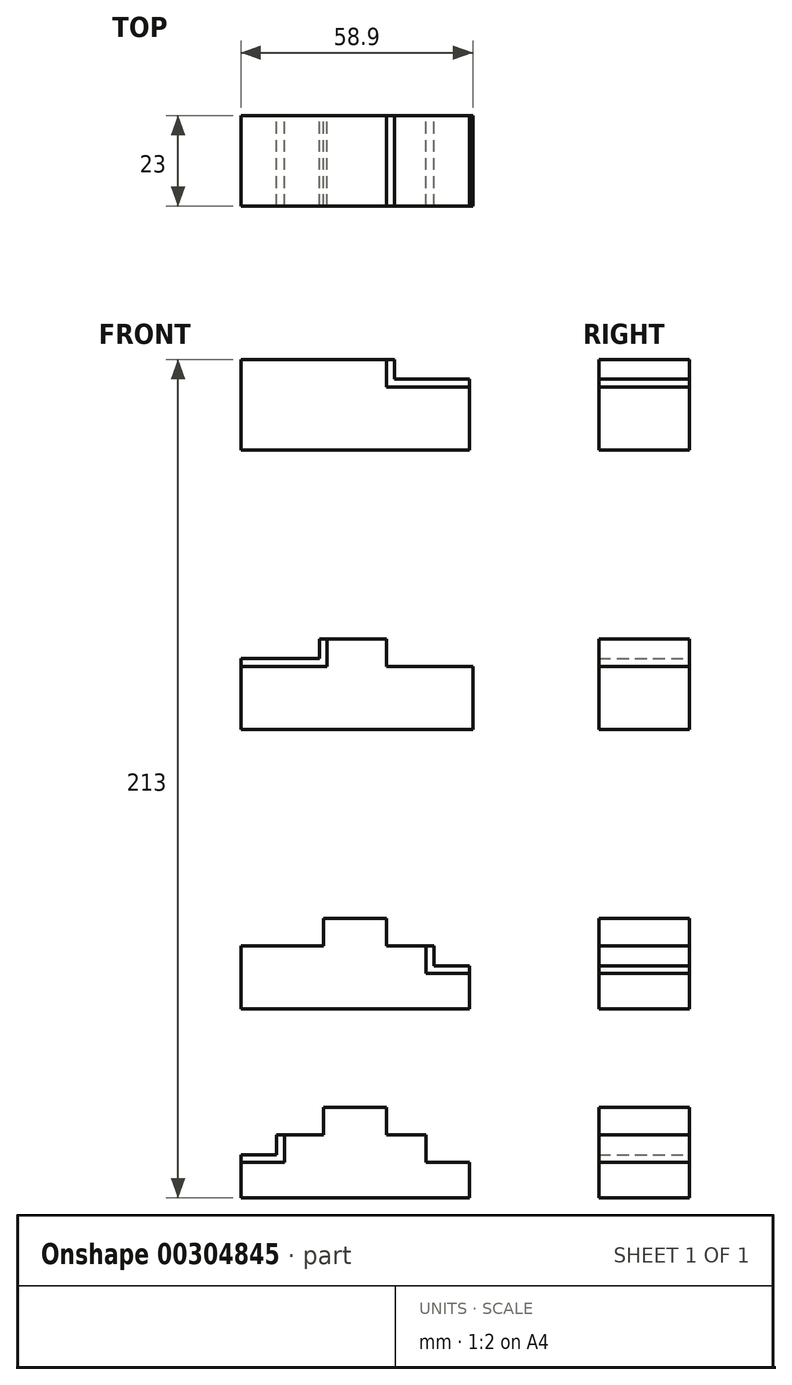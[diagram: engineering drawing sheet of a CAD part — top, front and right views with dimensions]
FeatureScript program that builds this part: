
annotation { "Feature Type Name" : "Feature", "Feature Type Description" : "" }
export const myFeature = defineFeature(function(context is Context, id is Id, definition is map)
    precondition{}
    {
        {
            var Q0;
            Q0=qCreatedBy(makeId("Front.planeOp"),FACE);
            var sketch = newSketch(context, id + "F0", { "sketchPlane" : qUnion([Q0])});
            skLineSegment(sketch, "E0.bottom", {"start": v(0, 0) * mm, "end": v(200, 0) * mm, "construction": true});
            skLineSegment(sketch, "E0.top", {"start": v(0, 300) * mm, "end": v(200, 300) * mm, "construction": true});
            skLineSegment(sketch, "E0.left", {"start": v(0, 0) * mm, "end": v(0, 300) * mm, "construction": true});
            skLineSegment(sketch, "E0.right", {"start": v(200, 0) * mm, "end": v(200, 300) * mm, "construction": true});
            skPoint(sketch, "E1", {"position": v(0, 200) * mm});
            skPoint(sketch, "E2", {"position": v(0, 100) * mm});
            skSolve(sketch);
        }
        {
            var Q0;
            Q0=qCreatedBy(makeId("Front.planeOp"),FACE);
            var sketch = newSketch(context, id + "F1", { "sketchPlane" : qUnion([Q0])});
            skLineSegment(sketch, "E3.bottom", {"start": v(30, 252) * mm, "end": v(88, 252) * mm});
            skLineSegment(sketch, "E3.top", {"start": v(30, 229) * mm, "end": v(88, 229) * mm});
            skLineSegment(sketch, "E3.left", {"start": v(30, 252) * mm, "end": v(30, 229) * mm});
            skLineSegment(sketch, "E3.right", {"start": v(88, 252) * mm, "end": v(88, 229) * mm});
            skLineSegment(sketch, "E4", {"start": v(69, 252) * mm, "end": v(69, 247) * mm});
            skLineSegment(sketch, "E5", {"start": v(69, 247) * mm, "end": v(88, 247) * mm});
            skLineSegment(sketch, "E6.0", {"start": v(67, 245) * mm, "end": v(88, 245) * mm});
            skLineSegment(sketch, "E6.1", {"start": v(67, 252) * mm, "end": v(67, 245) * mm});
            skSolve(sketch);
        }
        {
            var Q0;
            Q0=qCreatedBy(makeId("Front.planeOp"),FACE);
            var sketch = newSketch(context, id + "F2", { "sketchPlane" : qUnion([Q0])});
            skLineSegment(sketch, "E7.bottom", {"start": v(30, 181) * mm, "end": v(88.9, 181) * mm});
            skLineSegment(sketch, "E7.top", {"start": v(30, 158) * mm, "end": v(88.9, 158) * mm});
            skLineSegment(sketch, "E7.left", {"start": v(30, 181) * mm, "end": v(30, 158) * mm});
            skLineSegment(sketch, "E7.right", {"start": v(88.9, 181) * mm, "end": v(88.9, 158) * mm});
            skLineSegment(sketch, "E8", {"start": v(30, 176) * mm, "end": v(49.9, 176) * mm});
            skLineSegment(sketch, "E9", {"start": v(49.9, 176) * mm, "end": v(49.9, 181) * mm});
            skLineSegment(sketch, "E10.0", {"start": v(51.9, 174) * mm, "end": v(51.9, 181) * mm});
            skLineSegment(sketch, "E10.1", {"start": v(30, 174) * mm, "end": v(51.9, 174) * mm});
            skLineSegment(sketch, "E11", {"start": v(59.45, 154.93) * mm, "end": v(59.45, 132.57) * mm, "construction": true});
            skPoint(sketch, "E11.startSnap0", {"position": v(59.45, 158) * mm});
            skLineSegment(sketch, "E12.MirrorCS", {"start": v(67, 174) * mm, "end": v(67, 181) * mm});
            skLineSegment(sketch, "E13.MirrorCS", {"start": v(88.9, 174) * mm, "end": v(67, 174) * mm});
            skSolve(sketch);
        }
        {
            var Q0;
            Q0=qCreatedBy(makeId("Front.planeOp"),FACE);
            var sketch = newSketch(context, id + "F3", { "sketchPlane" : qUnion([Q0])});
            skLineSegment(sketch, "E14.bottom", {"start": v(30, 110) * mm, "end": v(88, 110) * mm});
            skLineSegment(sketch, "E14.top", {"start": v(30, 87) * mm, "end": v(88, 87) * mm});
            skLineSegment(sketch, "E14.left", {"start": v(30, 110) * mm, "end": v(30, 87) * mm});
            skLineSegment(sketch, "E14.right", {"start": v(88, 110) * mm, "end": v(88, 87) * mm});
            skLineSegment(sketch, "E15", {"start": v(67, 110) * mm, "end": v(67, 103) * mm});
            skLineSegment(sketch, "E16", {"start": v(67, 103) * mm, "end": v(77, 103) * mm});
            skLineSegment(sketch, "E17", {"start": v(77, 103) * mm, "end": v(77, 96) * mm});
            skLineSegment(sketch, "E18", {"start": v(77, 96) * mm, "end": v(88, 96) * mm});
            skLineSegment(sketch, "E19.0", {"start": v(79, 98) * mm, "end": v(88, 98) * mm});
            skLineSegment(sketch, "E19.1", {"start": v(79, 105) * mm, "end": v(79, 98) * mm});
            skLineSegment(sketch, "E19.2", {"start": v(69, 105) * mm, "end": v(79, 105) * mm});
            skLineSegment(sketch, "E19.3", {"start": v(69, 110.26) * mm, "end": v(69, 105) * mm});
            skLineSegment(sketch, "E20", {"start": v(77, 103) * mm, "end": v(79, 103) * mm});
            skLineSegment(sketch, "E21", {"start": v(59, 115.4) * mm, "end": v(59, 121.32) * mm, "construction": true});
            skPoint(sketch, "E21.startSnap0", {"position": v(59, 110) * mm});
            skLineSegment(sketch, "E22.MirrorCS", {"start": v(51, 110) * mm, "end": v(51, 103) * mm});
            skLineSegment(sketch, "E23.MirrorCS", {"start": v(51, 103) * mm, "end": v(41, 103) * mm});
            skLineSegment(sketch, "E24.MirrorCS", {"start": v(41, 103) * mm, "end": v(41, 96) * mm, "construction": true});
            skLineSegment(sketch, "E25.MirrorCS", {"start": v(41, 96) * mm, "end": v(30, 96) * mm});
            skLineSegment(sketch, "E26", {"start": v(41, 103) * mm, "end": v(30, 103) * mm});
            skLineSegment(sketch, "E27.0.1.0", {"start": v(41, 55) * mm, "end": v(41, 48) * mm});
            skLineSegment(sketch, "E27.0.1.1", {"start": v(67, 55) * mm, "end": v(77, 55) * mm});
            skLineSegment(sketch, "E27.0.1.2", {"start": v(77, 48) * mm, "end": v(88, 48) * mm});
            skLineSegment(sketch, "E27.0.1.3", {"start": v(51, 62) * mm, "end": v(51, 55) * mm});
            skLineSegment(sketch, "E27.0.1.4", {"start": v(30, 62) * mm, "end": v(88, 62) * mm});
            skLineSegment(sketch, "E27.0.1.5", {"start": v(51, 55) * mm, "end": v(41, 55) * mm});
            skPoint(sketch, "E27.0.1.6", {"position": v(59, 62) * mm});
            skLineSegment(sketch, "E27.0.1.7", {"start": v(30, 39) * mm, "end": v(88, 39) * mm});
            skLineSegment(sketch, "E27.0.1.8", {"start": v(88, 62) * mm, "end": v(88, 39) * mm});
            skLineSegment(sketch, "E27.0.1.9", {"start": v(30, 62) * mm, "end": v(30, 39) * mm});
            skLineSegment(sketch, "E27.0.1.10", {"start": v(41, 55) * mm, "end": v(30, 55) * mm, "construction": true});
            skLineSegment(sketch, "E27.0.1.11", {"start": v(79, 50) * mm, "end": v(88, 50) * mm});
            skLineSegment(sketch, "E27.0.1.12", {"start": v(69, 57) * mm, "end": v(79, 57) * mm});
            skLineSegment(sketch, "E27.0.1.13", {"start": v(41, 48) * mm, "end": v(30, 48) * mm});
            skLineSegment(sketch, "E27.0.1.14", {"start": v(67, 62) * mm, "end": v(67, 55) * mm});
            skLineSegment(sketch, "E27.0.1.15", {"start": v(69, 62.26) * mm, "end": v(69, 57) * mm});
            skLineSegment(sketch, "E27.0.1.16", {"start": v(77, 55) * mm, "end": v(77, 48) * mm});
            skLineSegment(sketch, "E27.0.1.17", {"start": v(79, 57) * mm, "end": v(79, 50) * mm});
            skLineSegment(sketch, "E27.0.1.18", {"start": v(77, 55) * mm, "end": v(79, 55) * mm});
            skLineSegment(sketch, "E27.direction1", {"start": v(30, 87) * mm, "end": v(120.8, 87) * mm, "construction": true});
            skLineSegment(sketch, "E27.direction2", {"start": v(30, 87) * mm, "end": v(30, 39) * mm, "construction": true});
            skLineSegment(sketch, "E28.MirrorCS", {"start": v(39, 57) * mm, "end": v(39, 50) * mm});
            skLineSegment(sketch, "E29.MirrorCS", {"start": v(49, 62.26) * mm, "end": v(49, 57) * mm});
            skLineSegment(sketch, "E30.MirrorCS", {"start": v(39, 50) * mm, "end": v(30, 50) * mm});
            skLineSegment(sketch, "E31.MirrorCS", {"start": v(41, 55) * mm, "end": v(39, 55) * mm});
            skLineSegment(sketch, "E32.MirrorCS", {"start": v(49, 57) * mm, "end": v(39, 57) * mm});
            skSolve(sketch);
        }
        {
            var Q0;
            Q0=makeQuery(id+"F1.imprint","IMPRINT",FACE,{"disambiguationData":[TD([[makeQuery(id+"F1.imprint","IMPRINT",EDGE,{"derivedFrom":sQuery(id+"F1.wireOp",EDGE,"K7ecBAno-6BI1-ZI8E-EF1z-YLERG8wcsJRb.bottom")}),-1.0]])]});
            var Q1;
            {var subQ1=sQuery(id+"F2.wireOp",EDGE,"E7.top");Q1=makeQuery(id+"F2.imprint","IMPRINT",FACE,{"disambiguationData":[TD([[makeQuery(id+"F2.imprint","IMPRINT",EDGE,{"derivedFrom":subQ1}),1.0]])]});}
            var Q2;
            {var subQ1=sQuery(id+"F1.wireOp",EDGE,"E3.top");Q2=makeQuery(id+"F1.imprint","IMPRINT",FACE,{"disambiguationData":[TD([[makeQuery(id+"F1.imprint","IMPRINT",EDGE,{"derivedFrom":subQ1}),1.0]])]});}
            var Q3;
            {var subQ5=sQuery(id+"F3.wireOp",EDGE,"E14.top");Q3=makeQuery(id+"F3.imprint","IMPRINT",FACE,{"disambiguationData":[TD([[makeQuery(id+"F3.imprint","IMPRINT",EDGE,{"derivedFrom":subQ5}),1.0]])]});}
            var Q4;
            Q4=makeQuery(id+"F3.imprint","IMPRINT",FACE,{"disambiguationData":[TD([[makeQuery(id+"F3.imprint","IMPRINT",EDGE,{"derivedFrom":sQuery(id+"F3.wireOp",EDGE,"E27.0.1.0")}),1.0]])]});
            extrude(context, id + "F4", {"entities" : qUnion([Q0, Q1, Q2, Q3, Q4]), "depth" : 23 * mm});
        }
        {
            var Q0;
            {var subQ0=sQuery(id+"F2.wireOp",EDGE,"E8");Q0=makeQuery(id+"F2.imprint","IMPRINT",FACE,{"disambiguationData":[TD([[makeQuery(id+"F2.imprint","IMPRINT",EDGE,{"derivedFrom":subQ0}),-1.0]])]});}
            var Q1;
            Q1=makeQuery(id+"F3.imprint","IMPRINT",FACE,{"disambiguationData":[TD([[makeQuery(id+"F3.imprint","IMPRINT",EDGE,{"derivedFrom":sQuery(id+"F3.wireOp",EDGE,"E17")}),1.0]])]});
            var Q2;
            Q2=makeQuery(id+"F3.imprint","IMPRINT",FACE,{"disambiguationData":[TD([[makeQuery(id+"F3.imprint","IMPRINT",EDGE,{"derivedFrom":sQuery(id+"F3.wireOp",EDGE,"E27.0.1.0")}),-1.0]])]});
            var Q3;
            {var subQ1=sQuery(id+"F1.wireOp",EDGE,"E4");Q3=makeQuery(id+"F1.imprint","IMPRINT",FACE,{"disambiguationData":[TD([[makeQuery(id+"F1.imprint","IMPRINT",EDGE,{"derivedFrom":subQ1}),-1.0]])]});}
            extrude(context, id + "F5", {"entities" : qUnion([Q0, Q1, Q2, Q3]), "depth" : 23 * mm});
        }
    });
